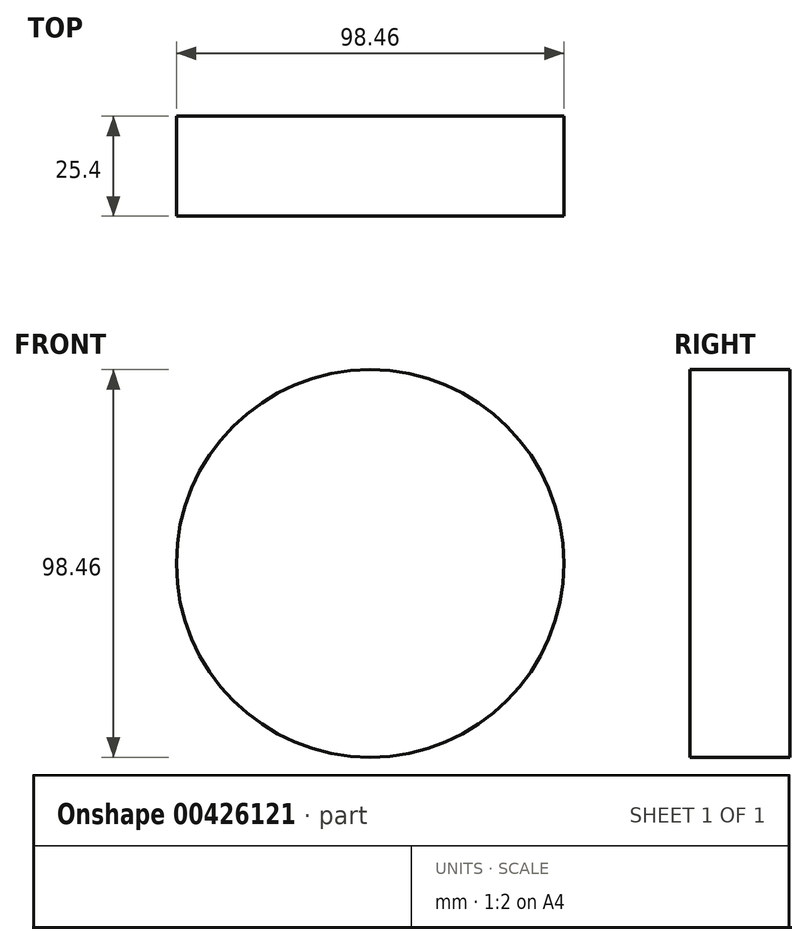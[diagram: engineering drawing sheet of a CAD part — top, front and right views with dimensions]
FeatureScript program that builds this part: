
annotation { "Feature Type Name" : "Feature", "Feature Type Description" : "" }
export const myFeature = defineFeature(function(context is Context, id is Id, definition is map)
    precondition{}
    {
        {
            var Q0;
            Q0=qCreatedBy(makeId("Front.planeOp"),FACE);
            var sketch = newSketch(context, id + "F0", { "sketchPlane" : qUnion([Q0])});
            skCircle(sketch, "E0", {"center": v(0, 0) * mm, "radius": 49.23 * mm});
            skSolve(sketch);
        }
        {
            var Q0;
            Q0=makeQuery(id+"F0.imprint","IMPRINT",FACE,{"disambiguationData":[TD([[makeQuery(id+"F0.imprint","IMPRINT",EDGE,{"derivedFrom":sQuery(id+"F0.wireOp",EDGE,"E0")}),1.0]])]});
            extrude(context, id + "F1", {"entities" : qUnion([Q0]), "depth" : 25.4 * mm});
        }
    });
